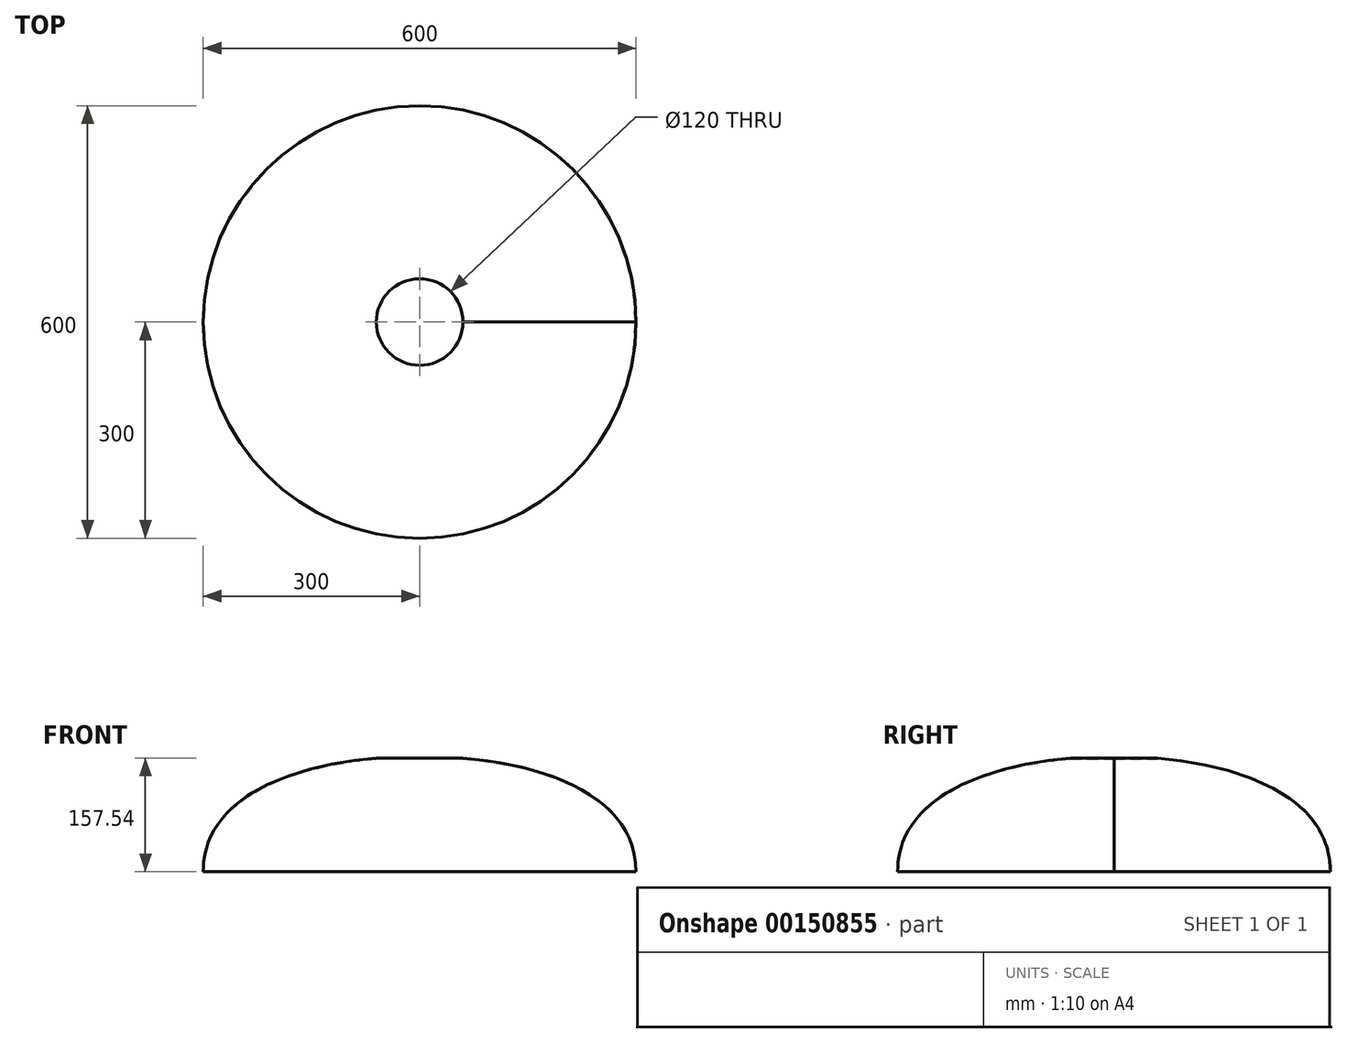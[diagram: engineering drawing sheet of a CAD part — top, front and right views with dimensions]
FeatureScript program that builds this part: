
annotation { "Feature Type Name" : "Feature", "Feature Type Description" : "" }
export const myFeature = defineFeature(function(context is Context, id is Id, definition is map)
    precondition{}
    {
        {
            var Q0;
            Q0=qCreatedBy(makeId("Right.planeOp"),FACE);
            var sketch = newSketch(context, id + "F0", { "sketchPlane" : qUnion([Q0])});
            skLineSegment(sketch, "E0", {"start": v(0, 0) * mm, "end": v(300, 0) * mm});
            skLineSegment(sketch, "E1", {"start": v(0, 160) * mm, "end": v(0, 0) * mm});
            skFitSpline(sketch, "E2", {"points": [v(0, 160) * mm, v(300, 0) * mm], "startDerivative": vector(480, 0) * mm, "endDerivative": vector(0, -330) * mm});
            skLineSegment(sketch, "E3", {"start": v(0, 160) * mm, "end": v(300, 160) * mm, "construction": true});
            skLineSegment(sketch, "E4", {"start": v(300, 160) * mm, "end": v(300, 0) * mm, "construction": true});
            skSolve(sketch);
        }
        {
            var Q0;
            Q0 = qSketchRegion(id + "F0", true);
            var Q1;
            Q1=sQuery(id+"F0.wireOp",EDGE,"E1");
            revolve(context, id + "F1", {"entities" : qUnion([Q0]), "axis" : qUnion([Q1]), "revolveType" : RevolveType.FULL});
        }
        {
            var Q0;
            Q0=makeQuery(id+"F1.opRevolve","SWEPT_FACE",FACE,{"disambiguationData":[OSD([sQuery(id+"F0.wireOp",EDGE,"E0")])]});
            shell(context, id + "F2", {"entities" : qUnion([Q0]), "thickness" : 1 * mm});
        }
        {
            var Q0;
            Q0=qCreatedBy(makeId("Top.planeOp"),FACE);
            var sketch = newSketch(context, id + "F3", { "sketchPlane" : qUnion([Q0])});
            skCircle(sketch, "E5", {"center": v(0, 0) * mm, "radius": 60 * mm});
            skSolve(sketch);
        }
        {
            var Q0;
            Q0 = qSketchRegion(id + "F3", true);
            extrude(context, id + "F4", {"entities" : qUnion([Q0]), "operationType" : NewBodyOperationType.REMOVE, "endBound" : BoundingType.THROUGH_ALL, "depth" : 25 * mm});
        }
    });
